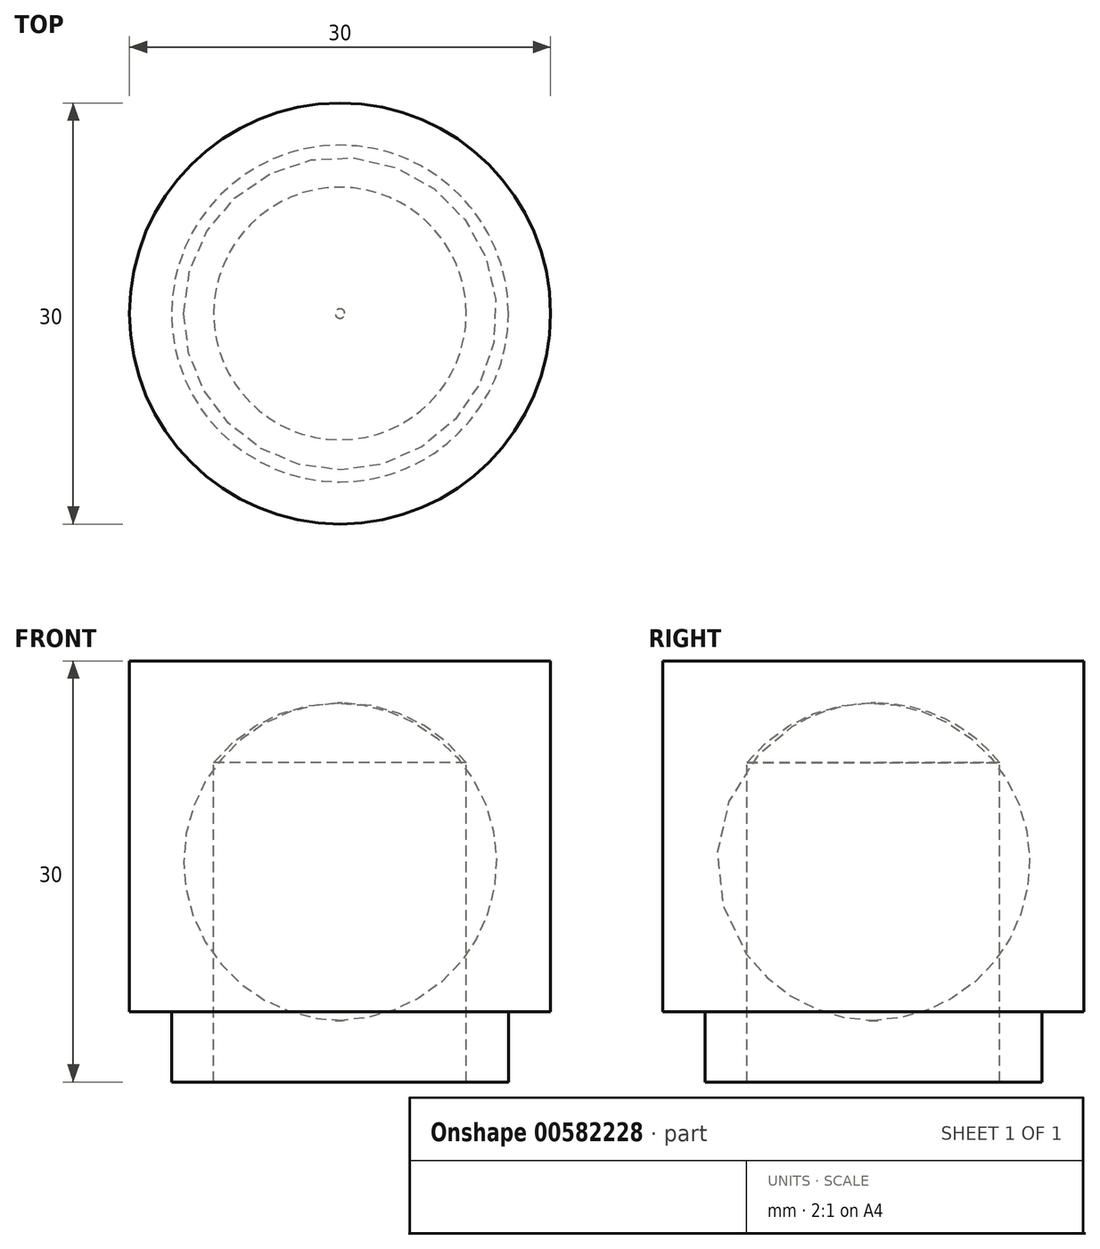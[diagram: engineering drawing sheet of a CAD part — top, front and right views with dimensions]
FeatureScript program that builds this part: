
annotation { "Feature Type Name" : "Feature", "Feature Type Description" : "" }
export const myFeature = defineFeature(function(context is Context, id is Id, definition is map)
    precondition{}
    {
        {
            var Q0;
            Q0=qCreatedBy(makeId("Front.planeOp"),FACE);
            var sketch = newSketch(context, id + "F0", { "sketchPlane" : qUnion([Q0]), "disableImprinting" : false});
            skLineSegment(sketch, "E0.MirrorCS", {"start": v(-12, -25) * mm, "end": v(-15, -25) * mm});
            skLineSegment(sketch, "E1", {"start": v(-15, -3) * mm, "end": v(-15, 0) * mm});
            skLineSegment(sketch, "E2", {"start": v(-15, -3) * mm, "end": v(-15, -25) * mm});
            skLineSegment(sketch, "E3", {"start": v(-12, -25) * mm, "end": v(-12, -30) * mm});
            skLineSegment(sketch, "E4", {"start": v(-12, -30) * mm, "end": v(-9, -30) * mm});
            skLineSegment(sketch, "E5", {"start": v(-15, 0) * mm, "end": v(0, 0) * mm});
            skLineSegment(sketch, "E6.MirrorCS", {"start": v(12, -25) * mm, "end": v(12, -30) * mm});
            skLineSegment(sketch, "E7.MirrorCS", {"start": v(15, 0) * mm, "end": v(0, 0) * mm});
            skLineSegment(sketch, "E8.MirrorCS", {"start": v(15, -3) * mm, "end": v(15, -25) * mm});
            skLineSegment(sketch, "E9.MirrorCS", {"start": v(12, -25) * mm, "end": v(15, -25) * mm});
            skLineSegment(sketch, "E10.MirrorCS", {"start": v(15, -3) * mm, "end": v(15, 0) * mm});
            skLineSegment(sketch, "E11.MirrorCS", {"start": v(12, -30) * mm, "end": v(9, -30) * mm});
            skArc(sketch, "E12", {"start": v(9, -7.69) * mm, "mid": v(0.11, -3) * mm, "end": v(-9, -7.24) * mm});
            skLineSegment(sketch, "E13", {"start": v(-9, -30) * mm, "end": v(-9, -7.24) * mm});
            skLineSegment(sketch, "E14", {"start": v(9, -30) * mm, "end": v(9, -7.69) * mm});
            skLineSegment(sketch, "E15", {"start": v(0, 0) * mm, "end": v(0, -3) * mm});
            skSolve(sketch);
        }
        {
            var Q0;
            {var subQ0=sQuery(id+"F0.wireOp",EDGE,"I7DhDJuf-7NLr-Svl4-PwQn-US4yEfDLbxPE.left");Q0=makeQuery(id+"F0.imprint","IMPRINT",FACE,{"disambiguationData":[TD([[makeQuery(id+"F0.imprint","IMPRINT",EDGE,{"derivedFrom":subQ0}),-1.0]])]});}
            var Q1;
            Q1=makeQuery(id+"F0.imprint","IMPRINT",FACE,{"disambiguationData":[TD([[makeQuery(id+"F0.imprint","IMPRINT",EDGE,{"derivedFrom":sQuery(id+"F0.wireOp",EDGE,"32eac864-653d-4b33-877a-62f6442f8a590.MirrorCS")}),1.0]])]});
            var Q2;
            Q2=makeQuery(id+"F0.imprint","IMPRINT",FACE,{"disambiguationData":[TD([[makeQuery(id+"F0.imprint","IMPRINT",EDGE,{"derivedFrom":sQuery(id+"F0.wireOp",EDGE,"E0.MirrorCS")}),-1.0]])]});
            var Q3;
            Q3=sQuery(id+"F0.wireOp",EDGE,"E15");
            revolve(context, id + "F1", {"entities" : qUnion([Q0, Q1, Q2]), "axis" : qUnion([Q3]), "revolveType" : RevolveType.FULL});
        }
    });
